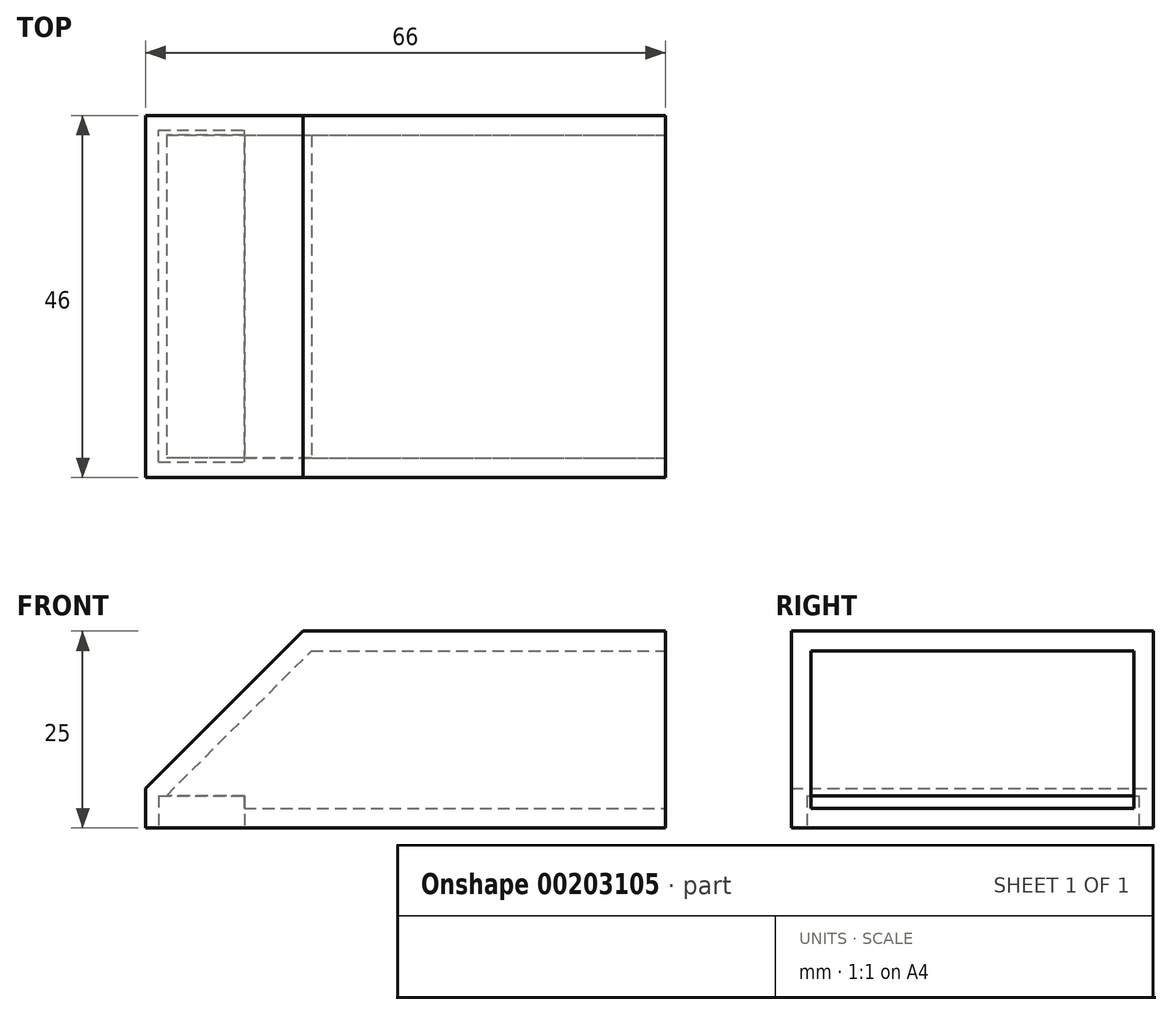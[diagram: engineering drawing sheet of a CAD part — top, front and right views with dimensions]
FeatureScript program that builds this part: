
annotation { "Feature Type Name" : "Feature", "Feature Type Description" : "" }
export const myFeature = defineFeature(function(context is Context, id is Id, definition is map)
    precondition{}
    {
        {
            var Q0;
            Q0=qCreatedBy(makeId("Top.planeOp"),FACE);
            var sketch = newSketch(context, id + "F0", { "sketchPlane" : qUnion([Q0])});
            skLineSegment(sketch, "E0.bottom", {"start": v(0, 23) * mm, "end": v(66, 23) * mm});
            skLineSegment(sketch, "E0.top", {"start": v(0, -23) * mm, "end": v(66, -23) * mm});
            skLineSegment(sketch, "E0.left", {"start": v(0, 23) * mm, "end": v(0, -23) * mm});
            skLineSegment(sketch, "E0.right", {"start": v(66, 23) * mm, "end": v(66, -23) * mm});
            skSolve(sketch);
        }
        {
            var Q0;
            Q0=makeQuery(id+"F0.imprint","IMPRINT",FACE,{"disambiguationData":[TD([[makeQuery(id+"F0.imprint","IMPRINT",EDGE,{"derivedFrom":sQuery(id+"F0.wireOp",EDGE,"E0.bottom")}),-1.0]])]});
            extrude(context, id + "F1", {"entities" : qUnion([Q0]), "depth" : 25 * mm});
        }
        {
            var Q0;
            Q0=makeQuery(id+"F1.opExtrude","CAP_EDGE",EDGE,{"disambiguationData":[OSD([sQuery(id+"F0.wireOp",EDGE,"E0.left")])],"isStart":false});
            chamfer(context, id + "F2", {"entities" : qUnion([Q0]), "width" : 20 * mm, "tangentPropagation" : true});
        }
        {
            var Q0;
            Q0=makeQuery(id+"F1.opExtrude","SWEPT_FACE",FACE,{"disambiguationData":[OSD([sQuery(id+"F0.wireOp",EDGE,"E0.right")])]});
            shell(context, id + "F3", {"entities" : qUnion([Q0]), "thickness" : 2.5 * mm});
        }
        {
            var Q0;
            Q0=makeQuery(id+"F1.opExtrude","CAP_FACE",FACE,{"disambiguationData":[OSD([sQuery(id+"F0.wireOp",EDGE,"E0.bottom"),sQuery(id+"F0.wireOp",EDGE,"E0.top"),sQuery(id+"F0.wireOp",EDGE,"E0.left"),sQuery(id+"F0.wireOp",EDGE,"E0.right")])],"isStart":true});
            var sketch = newSketch(context, id + "F4", { "sketchPlane" : qUnion([Q0])});
            skLineSegment(sketch, "E1.bottom", {"start": v(1.65, 21.03) * mm, "end": v(12.54, 21.03) * mm});
            skLineSegment(sketch, "E1.top", {"start": v(1.65, -21.15) * mm, "end": v(12.54, -21.15) * mm});
            skLineSegment(sketch, "E1.left", {"start": v(1.65, 21.03) * mm, "end": v(1.65, -21.15) * mm});
            skLineSegment(sketch, "E1.right", {"start": v(12.54, 21.03) * mm, "end": v(12.54, -21.15) * mm});
            skSolve(sketch);
        }
        {
            var Q0;
            Q0=makeQuery(id+"F4.imprint","IMPRINT",FACE,{"disambiguationData":[TD([[makeQuery(id+"F4.imprint","IMPRINT",EDGE,{"derivedFrom":sQuery(id+"F4.wireOp",EDGE,"E1.bottom")}),-1.0]])]});
            extrude(context, id + "F5", {"entities" : qUnion([Q0]), "operationType" : NewBodyOperationType.REMOVE, "oppositeDirection" : true, "depth" : 4.1 * mm});
        }
    });
